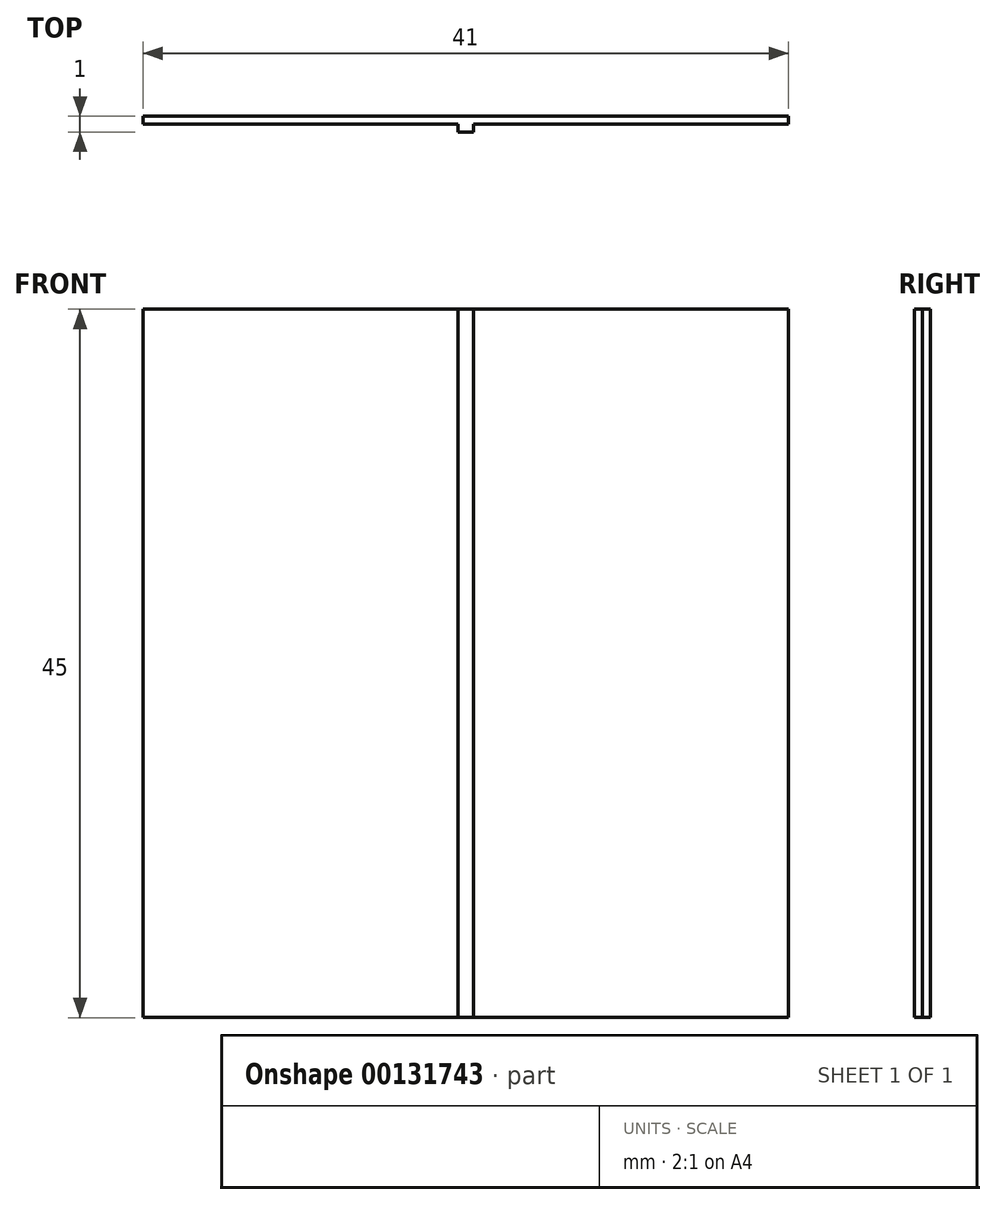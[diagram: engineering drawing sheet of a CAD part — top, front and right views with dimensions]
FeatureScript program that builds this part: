
annotation { "Feature Type Name" : "Feature", "Feature Type Description" : "" }
export const myFeature = defineFeature(function(context is Context, id is Id, definition is map)
    precondition{}
    {
        {
            var Q0;
            Q0=qCreatedBy(makeId("Front.planeOp"),FACE);
            var sketch = newSketch(context, id + "F0", { "sketchPlane" : qUnion([Q0])});
            skLineSegment(sketch, "E0.bottom", {"start": v(-566.24, 93.58) * mm, "end": v(-525.24, 93.58) * mm});
            skLineSegment(sketch, "E0.top", {"start": v(-566.24, 48.58) * mm, "end": v(-525.24, 48.58) * mm});
            skLineSegment(sketch, "E0.left", {"start": v(-566.24, 93.58) * mm, "end": v(-566.24, 48.58) * mm});
            skLineSegment(sketch, "E0.right", {"start": v(-525.24, 93.58) * mm, "end": v(-525.24, 48.58) * mm});
            skSolve(sketch);
        }
        {
            var Q0;
            Q0 = qSketchRegion(id + "F0", true);
            extrude(context, id + "F1", {"entities" : qUnion([Q0]), "depth" : .5 * mm});
        }
        {
            var Q0;
            Q0=makeQuery(id+"F1.opExtrude","CAP_FACE",FACE,{"disambiguationData":[OSD([sQuery(id+"F0.wireOp",EDGE,"E0.bottom"),sQuery(id+"F0.wireOp",EDGE,"E0.top"),sQuery(id+"F0.wireOp",EDGE,"E0.left"),sQuery(id+"F0.wireOp",EDGE,"E0.right")])],"isStart":false});
            var sketch = newSketch(context, id + "F2", { "sketchPlane" : qUnion([Q0])});
            skLineSegment(sketch, "E1.bottom", {"start": v(-546.24, 93.58) * mm, "end": v(-545.24, 93.58) * mm});
            skLineSegment(sketch, "E1.top", {"start": v(-546.24, 48.58) * mm, "end": v(-545.24, 48.58) * mm});
            skLineSegment(sketch, "E1.left", {"start": v(-546.24, 93.58) * mm, "end": v(-546.24, 48.58) * mm});
            skLineSegment(sketch, "E1.right", {"start": v(-545.24, 93.58) * mm, "end": v(-545.24, 48.58) * mm});
            skSolve(sketch);
        }
        {
            var Q0;
            Q0 = qSketchRegion(id + "F2", true);
            extrude(context, id + "F3", {"entities" : qUnion([Q0]), "operationType" : NewBodyOperationType.ADD, "depth" : .5 * mm});
        }
    });
